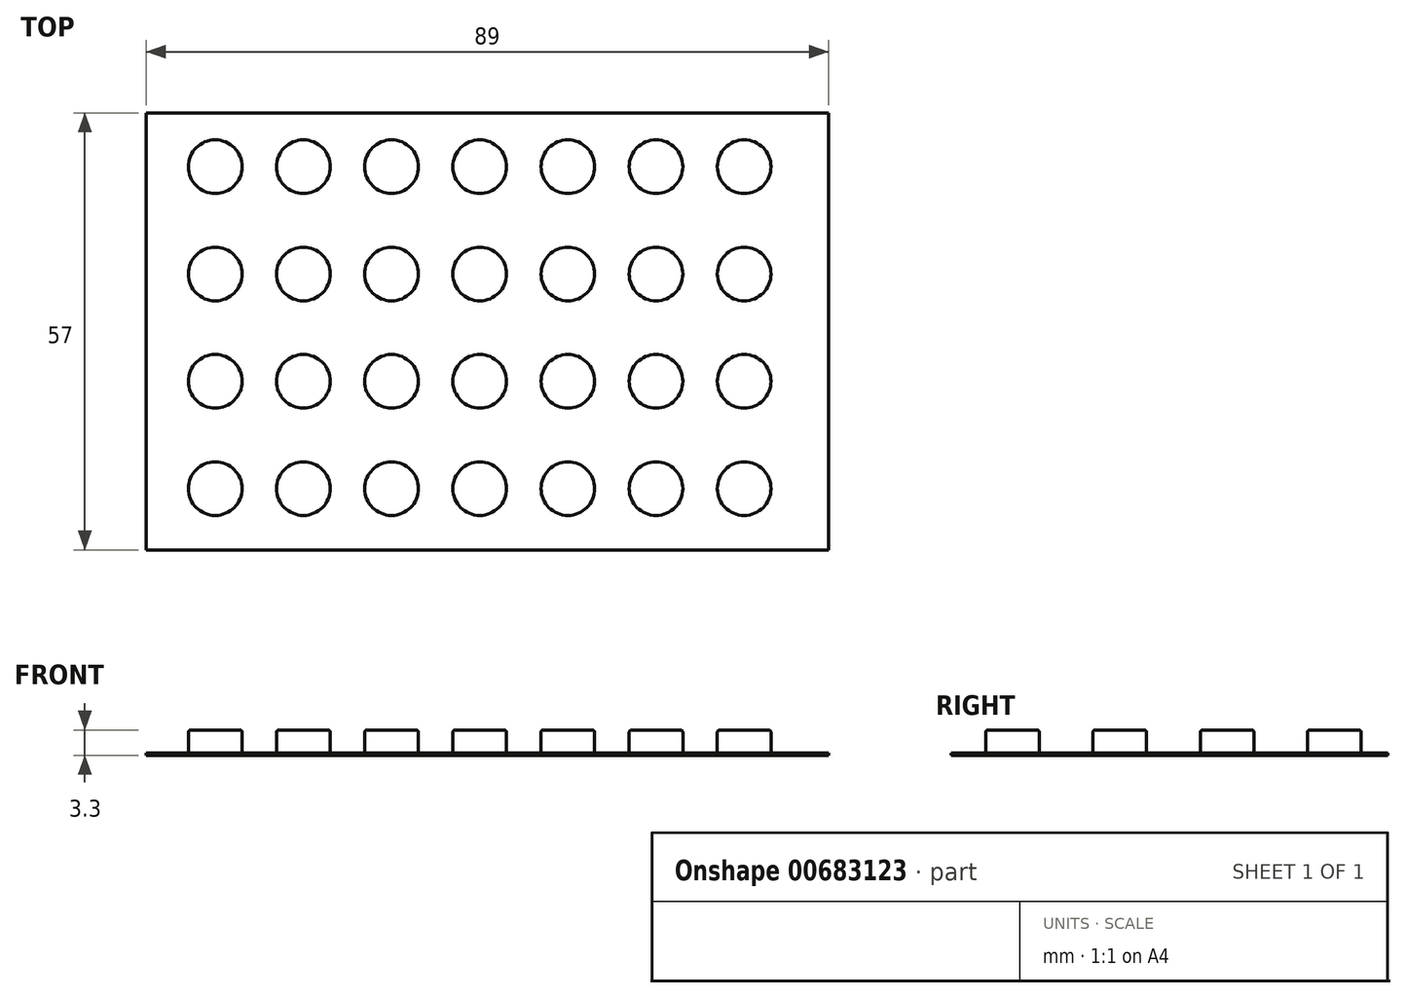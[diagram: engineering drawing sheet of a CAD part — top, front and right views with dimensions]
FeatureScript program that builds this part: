
annotation { "Feature Type Name" : "Feature", "Feature Type Description" : "" }
export const myFeature = defineFeature(function(context is Context, id is Id, definition is map)
    precondition{}
    {
        {
            var Q0;
            Q0=qCreatedBy(makeId("Top.planeOp"),FACE);
            var sketch = newSketch(context, id + "F0", { "sketchPlane" : qUnion([Q0])});
            skLineSegment(sketch, "E0.bottom", {"start": v(44.5, 28.5) * mm, "end": v(-44.5, 28.5) * mm});
            skLineSegment(sketch, "E0.top", {"start": v(44.5, -28.5) * mm, "end": v(-44.5, -28.5) * mm});
            skLineSegment(sketch, "E0.left", {"start": v(44.5, 28.5) * mm, "end": v(44.5, -28.5) * mm});
            skLineSegment(sketch, "E0.right", {"start": v(-44.5, 28.5) * mm, "end": v(-44.5, -28.5) * mm});
            skPoint(sketch, "E0.middle", {"position": v(0, 0) * mm});
            skSolve(sketch);
        }
        {
            var Q0;
            Q0=makeQuery(id+"F0.imprint","IMPRINT",FACE,{"disambiguationData":[TD([[makeQuery(id+"F0.imprint","IMPRINT",EDGE,{"derivedFrom":sQuery(id+"F0.wireOp",EDGE,"E0.bottom")}),1.0]])]});
            extrude(context, id + "F1", {"entities" : qUnion([Q0]), "depth" : .3 * mm, "offsetDistance" : 25 * mm});
        }
        {
            var Q0;
            Q0=makeQuery(id+"F1.opExtrude","CAP_FACE",FACE,{"disambiguationData":[OSD([sQuery(id+"F0.wireOp",EDGE,"E0.bottom"),sQuery(id+"F0.wireOp",EDGE,"E0.top"),sQuery(id+"F0.wireOp",EDGE,"E0.left"),sQuery(id+"F0.wireOp",EDGE,"E0.right")])],"isStart":false});
            var sketch = newSketch(context, id + "F2", { "sketchPlane" : qUnion([Q0])});
            skCircle(sketch, "E1", {"center": v(-35.5, 21.5) * mm, "radius": 3.5 * mm});
            skCircle(sketch, "E2.0.1.0", {"center": v(-35.5, 7.5) * mm, "radius": 3.5 * mm});
            skCircle(sketch, "E2.0.2.0", {"center": v(-35.5, -6.5) * mm, "radius": 3.5 * mm});
            skCircle(sketch, "E2.0.3.0", {"center": v(-35.5, -20.5) * mm, "radius": 3.5 * mm});
            skCircle(sketch, "E2.1.0.0", {"center": v(-24, 21.5) * mm, "radius": 3.5 * mm});
            skCircle(sketch, "E2.1.1.0", {"center": v(-24, 7.5) * mm, "radius": 3.5 * mm});
            skCircle(sketch, "E2.1.2.0", {"center": v(-24, -6.5) * mm, "radius": 3.5 * mm});
            skCircle(sketch, "E2.1.3.0", {"center": v(-24, -20.5) * mm, "radius": 3.5 * mm});
            skCircle(sketch, "E2.2.0.0", {"center": v(-12.5, 21.5) * mm, "radius": 3.5 * mm});
            skCircle(sketch, "E2.2.1.0", {"center": v(-12.5, 7.5) * mm, "radius": 3.5 * mm});
            skCircle(sketch, "E2.2.2.0", {"center": v(-12.5, -6.5) * mm, "radius": 3.5 * mm});
            skCircle(sketch, "E2.2.3.0", {"center": v(-12.5, -20.5) * mm, "radius": 3.5 * mm});
            skCircle(sketch, "E2.3.0.0", {"center": v(-1, 21.5) * mm, "radius": 3.5 * mm});
            skCircle(sketch, "E2.3.1.0", {"center": v(-1, 7.5) * mm, "radius": 3.5 * mm});
            skCircle(sketch, "E2.3.2.0", {"center": v(-1, -6.5) * mm, "radius": 3.5 * mm});
            skCircle(sketch, "E2.3.3.0", {"center": v(-1, -20.5) * mm, "radius": 3.5 * mm});
            skCircle(sketch, "E2.4.0.0", {"center": v(10.5, 21.5) * mm, "radius": 3.5 * mm});
            skCircle(sketch, "E2.4.1.0", {"center": v(10.5, 7.5) * mm, "radius": 3.5 * mm});
            skCircle(sketch, "E2.4.2.0", {"center": v(10.5, -6.5) * mm, "radius": 3.5 * mm});
            skCircle(sketch, "E2.4.3.0", {"center": v(10.5, -20.5) * mm, "radius": 3.5 * mm});
            skCircle(sketch, "E2.5.0.0", {"center": v(22, 21.5) * mm, "radius": 3.5 * mm});
            skCircle(sketch, "E2.5.1.0", {"center": v(22, 7.5) * mm, "radius": 3.5 * mm});
            skCircle(sketch, "E2.5.2.0", {"center": v(22, -6.5) * mm, "radius": 3.5 * mm});
            skCircle(sketch, "E2.5.3.0", {"center": v(22, -20.5) * mm, "radius": 3.5 * mm});
            skLineSegment(sketch, "E2.direction1", {"start": v(-35.5, 21.5) * mm, "end": v(-24, 21.5) * mm, "construction": true});
            skLineSegment(sketch, "E2.direction2", {"start": v(-35.5, 21.5) * mm, "end": v(-35.5, 7.5) * mm, "construction": true});
            skCircle(sketch, "E3.0.6.0", {"center": v(33.5, 21.5) * mm, "radius": 3.5 * mm});
            skCircle(sketch, "E3.0.6.1", {"center": v(33.5, 7.5) * mm, "radius": 3.5 * mm});
            skCircle(sketch, "E3.0.6.2", {"center": v(33.5, -6.5) * mm, "radius": 3.5 * mm});
            skCircle(sketch, "E3.0.6.3", {"center": v(33.5, -20.5) * mm, "radius": 3.5 * mm});
            skSolve(sketch);
        }
        {
            var Q0;
            Q0 = qSketchRegion(id + "F2", true);
            extrude(context, id + "F3", {"entities" : qUnion([Q0]), "operationType" : NewBodyOperationType.ADD, "depth" : 3 * mm, "offsetDistance" : 25 * mm});
        }
        {
            var Q0;
            Q0=makeQuery(id+"F3.opExtrude","CAP_EDGE",EDGE,{"disambiguationData":[OSD([sQuery(id+"F2.wireOp",EDGE,"E1")])],"isStart":false});
            var Q1;
            Q1=makeQuery(id+"F3.opExtrude","CAP_EDGE",EDGE,{"disambiguationData":[OSD([sQuery(id+"F2.wireOp",EDGE,"E2.1.0.0")])],"isStart":false});
            var Q2;
            Q2=makeQuery(id+"F3.opExtrude","CAP_FACE",FACE,{"disambiguationData":[OSD([sQuery(id+"F2.wireOp",EDGE,"E2.2.0.0")])],"isStart":false});
            var Q3;
            Q3=makeQuery(id+"F3.opExtrude","CAP_EDGE",EDGE,{"disambiguationData":[OSD([sQuery(id+"F2.wireOp",EDGE,"E2.2.0.0")])],"isStart":false});
            var Q4;
            Q4=makeQuery(id+"F3.opExtrude","CAP_EDGE",EDGE,{"disambiguationData":[OSD([sQuery(id+"F2.wireOp",EDGE,"E2.3.0.0")])],"isStart":false});
            var Q5;
            Q5=makeQuery(id+"F3.opExtrude","CAP_EDGE",EDGE,{"disambiguationData":[OSD([sQuery(id+"F2.wireOp",EDGE,"E2.4.0.0")])],"isStart":false});
            var Q6;
            Q6=makeQuery(id+"F3.opExtrude","CAP_EDGE",EDGE,{"disambiguationData":[OSD([sQuery(id+"F2.wireOp",EDGE,"E2.5.0.0")])],"isStart":false});
            var Q7;
            Q7=makeQuery(id+"F3.opExtrude","CAP_EDGE",EDGE,{"disambiguationData":[OSD([sQuery(id+"F2.wireOp",EDGE,"E2.5.1.0")])],"isStart":false});
            var Q8;
            Q8=makeQuery(id+"F3.opExtrude","CAP_EDGE",EDGE,{"disambiguationData":[OSD([sQuery(id+"F2.wireOp",EDGE,"E2.4.1.0")])],"isStart":false});
            var Q9;
            Q9=makeQuery(id+"F3.opExtrude","CAP_EDGE",EDGE,{"disambiguationData":[OSD([sQuery(id+"F2.wireOp",EDGE,"E2.3.1.0")])],"isStart":false});
            var Q10;
            Q10=makeQuery(id+"F3.opExtrude","CAP_EDGE",EDGE,{"disambiguationData":[OSD([sQuery(id+"F2.wireOp",EDGE,"E2.2.1.0")])],"isStart":false});
            var Q11;
            Q11=makeQuery(id+"F3.opExtrude","CAP_EDGE",EDGE,{"disambiguationData":[OSD([sQuery(id+"F2.wireOp",EDGE,"E2.1.1.0")])],"isStart":false});
            var Q12;
            Q12=makeQuery(id+"F3.opExtrude","CAP_EDGE",EDGE,{"disambiguationData":[OSD([sQuery(id+"F2.wireOp",EDGE,"E2.0.1.0")])],"isStart":false});
            var Q13;
            Q13=makeQuery(id+"F3.opExtrude","CAP_EDGE",EDGE,{"disambiguationData":[OSD([sQuery(id+"F2.wireOp",EDGE,"E2.0.2.0")])],"isStart":false});
            var Q14;
            Q14=makeQuery(id+"F3.opExtrude","CAP_EDGE",EDGE,{"disambiguationData":[OSD([sQuery(id+"F2.wireOp",EDGE,"E2.2.2.0")])],"isStart":false});
            var Q15;
            Q15=makeQuery(id+"F3.opExtrude","CAP_EDGE",EDGE,{"disambiguationData":[OSD([sQuery(id+"F2.wireOp",EDGE,"E2.3.2.0")])],"isStart":false});
            var Q16;
            Q16=makeQuery(id+"F3.opExtrude","CAP_EDGE",EDGE,{"disambiguationData":[OSD([sQuery(id+"F2.wireOp",EDGE,"E2.5.2.0")])],"isStart":false});
            var Q17;
            Q17=makeQuery(id+"F3.opExtrude","CAP_EDGE",EDGE,{"disambiguationData":[OSD([sQuery(id+"F2.wireOp",EDGE,"E2.4.2.0")])],"isStart":false});
            var Q18;
            Q18=makeQuery(id+"F3.opExtrude","CAP_EDGE",EDGE,{"disambiguationData":[OSD([sQuery(id+"F2.wireOp",EDGE,"E2.5.3.0")])],"isStart":false});
            var Q19;
            Q19=makeQuery(id+"F3.opExtrude","CAP_EDGE",EDGE,{"disambiguationData":[OSD([sQuery(id+"F2.wireOp",EDGE,"E2.4.3.0")])],"isStart":false});
            var Q20;
            Q20=makeQuery(id+"F3.opExtrude","CAP_EDGE",EDGE,{"disambiguationData":[OSD([sQuery(id+"F2.wireOp",EDGE,"E2.3.3.0")])],"isStart":false});
            var Q21;
            Q21=makeQuery(id+"F3.opExtrude","CAP_EDGE",EDGE,{"disambiguationData":[OSD([sQuery(id+"F2.wireOp",EDGE,"E2.2.3.0")])],"isStart":false});
            var Q22;
            Q22=makeQuery(id+"F3.opExtrude","CAP_EDGE",EDGE,{"disambiguationData":[OSD([sQuery(id+"F2.wireOp",EDGE,"E2.1.3.0")])],"isStart":false});
            var Q23;
            Q23=makeQuery(id+"F3.opExtrude","CAP_EDGE",EDGE,{"disambiguationData":[OSD([sQuery(id+"F2.wireOp",EDGE,"E2.0.3.0")])],"isStart":false});
            var Q24;
            Q24=makeQuery(id+"F3.opExtrude","CAP_EDGE",EDGE,{"disambiguationData":[OSD([sQuery(id+"F2.wireOp",EDGE,"E2.1.2.0")])],"isStart":false});
            var Q25;
            Q25=makeQuery(id+"F3.opExtrude","CAP_EDGE",EDGE,{"disambiguationData":[OSD([sQuery(id+"F2.wireOp",EDGE,"E3.0.6.3")])],"isStart":false});
            var Q26;
            Q26=makeQuery(id+"F3.opExtrude","CAP_EDGE",EDGE,{"disambiguationData":[OSD([sQuery(id+"F2.wireOp",EDGE,"E3.0.6.2")])],"isStart":false});
            var Q27;
            Q27=makeQuery(id+"F3.opExtrude","CAP_EDGE",EDGE,{"disambiguationData":[OSD([sQuery(id+"F2.wireOp",EDGE,"E3.0.6.1")])],"isStart":false});
            var Q28;
            Q28=makeQuery(id+"F3.opExtrude","CAP_EDGE",EDGE,{"disambiguationData":[OSD([sQuery(id+"F2.wireOp",EDGE,"E3.0.6.0")])],"isStart":false});
            fillet(context, id + "F4", {"entities" : qUnion([Q0, Q1, Q2, Q3, Q4, Q5, Q6, Q7, Q8, Q9, Q10, Q11, Q12, Q13, Q14, Q15, Q16, Q17, Q18, Q19, Q20, Q21, Q22, Q23, Q24, Q25, Q26, Q27, Q28]), "radius" : .3 * mm, "tangentPropagation" : true, "allowEdgeOverflow" : false});
        }
        {
            var Q0;
            Q0 = qSketchRegion(id + "F2", true);
            extrude(context, id + "F5", {"entities" : qUnion([Q0]), "operationType" : NewBodyOperationType.ADD, "depth" : 2.5 * mm, "offsetDistance" : 25 * mm});
        }
    });
